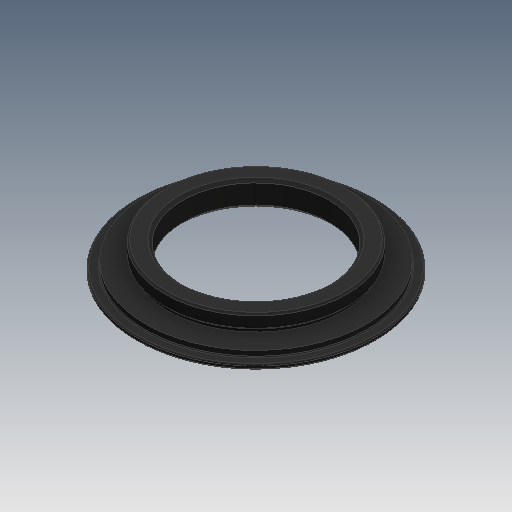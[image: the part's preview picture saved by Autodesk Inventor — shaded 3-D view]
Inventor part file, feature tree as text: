
AUTODESK INVENTOR PART (.ipt)
format: ipt  version: 2019 (Build 230136000, 136)  size: 185,856 bytes
history: native  units: mm
features: fillet x1
ambient origin geometry x8: Origin, YZ Plane, XZ Plane, XY Plane, X Axis, Y Axis, Z Axis, Center Point
bodies: Solid1 (feature_tree)
feature tree (1):
  fillet  "Fillet2"  [1 undecoded]
note: 1 required parameter value undecoded (feature->parameter linkage not recoverable at this tier; creation-order binding heuristic only, values carry confidence <= 0.55)
